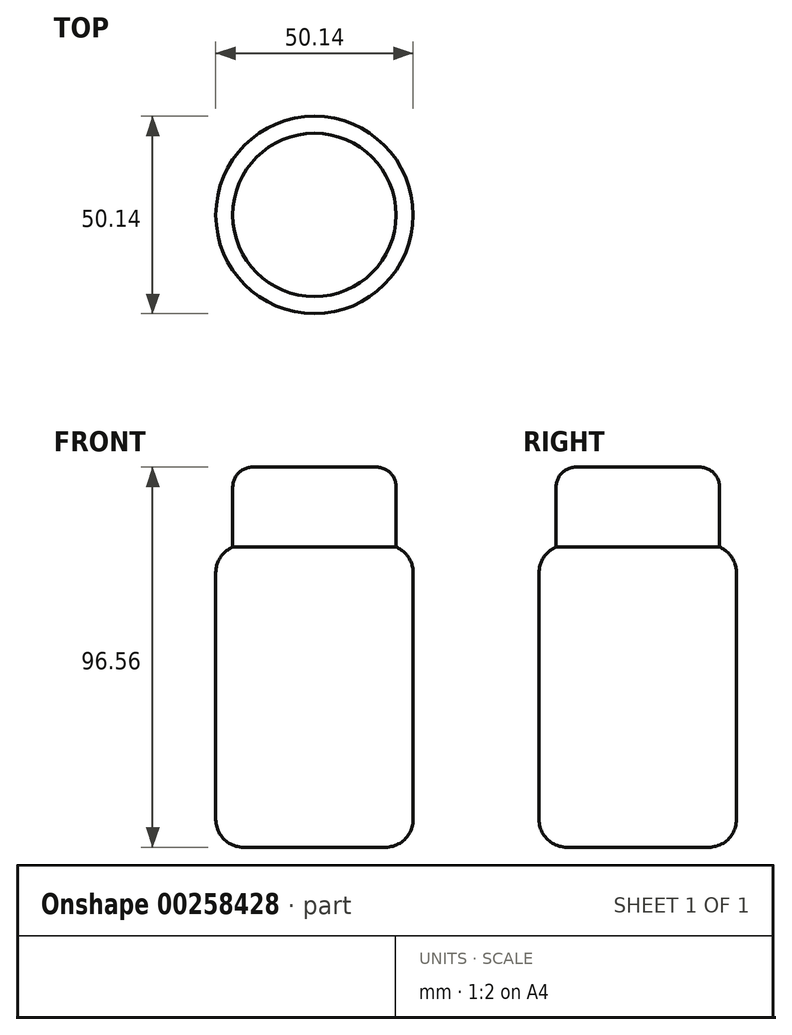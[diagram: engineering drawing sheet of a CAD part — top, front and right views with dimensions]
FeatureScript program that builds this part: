
annotation { "Feature Type Name" : "Feature", "Feature Type Description" : "" }
export const myFeature = defineFeature(function(context is Context, id is Id, definition is map)
    precondition{}
    {
        {
            var Q0;
            Q0=qCreatedBy(makeId("Top.planeOp"),FACE);
            var sketch = newSketch(context, id + "F0", { "sketchPlane" : qUnion([Q0])});
            skCircle(sketch, "E0", {"center": v(0, 0) * mm, "radius": 25.07 * mm});
            skSolve(sketch);
        }
        {
            var Q0;
            Q0=makeQuery(id+"F0.imprint","IMPRINT",FACE,{"disambiguationData":[TD([[makeQuery(id+"F0.imprint","IMPRINT",EDGE,{"derivedFrom":sQuery(id+"F0.wireOp",EDGE,"E0")}),1.0]])]});
            extrude(context, id + "F1", {"entities" : qUnion([Q0]), "depth" : 76.26 * mm, "symmetric" : true});
        }
        {
            var Q0;
            Q0=makeQuery(id+"F1.opExtrude","CAP_FACE",FACE,{"disambiguationData":[OSD([sQuery(id+"F0.wireOp",EDGE,"E0")])],"isStart":false});
            var sketch = newSketch(context, id + "F2", { "sketchPlane" : qUnion([Q0])});
            skCircle(sketch, "E1", {"center": v(0, 0) * mm, "radius": 20.75 * mm});
            skSolve(sketch);
        }
        {
            var Q0;
            Q0=makeQuery(id+"F2.imprint","IMPRINT",FACE,{"disambiguationData":[TD([[makeQuery(id+"F2.imprint","IMPRINT",EDGE,{"derivedFrom":sQuery(id+"F2.wireOp",EDGE,"E1")}),1.0]])]});
            extrude(context, id + "F3", {"entities" : qUnion([Q0]), "operationType" : NewBodyOperationType.ADD, "depth" : 20.3 * mm});
        }
        {
            var Q0;
            Q0=makeQuery(id+"F1.opExtrude","CAP_EDGE",EDGE,{"disambiguationData":[OSD([sQuery(id+"F0.wireOp",EDGE,"E0")])],"isStart":false});
            var Q1;
            Q1=makeQuery(id+"F1.opExtrude","CAP_EDGE",EDGE,{"disambiguationData":[OSD([sQuery(id+"F0.wireOp",EDGE,"E0")])],"isStart":true});
            fillet(context, id + "F4", {"entities" : qUnion([Q0, Q1]), "radius" : 7 * mm, "tangentPropagation" : true, "allowEdgeOverflow" : false});
        }
        {
            var Q0;
            Q0=makeQuery(id+"F3.opExtrude","CAP_EDGE",EDGE,{"disambiguationData":[OSD([sQuery(id+"F2.wireOp",EDGE,"E1")])],"isStart":false});
            fillet(context, id + "F5", {"entities" : qUnion([Q0]), "radius" : 5 * mm, "tangentPropagation" : true, "allowEdgeOverflow" : false});
        }
    });
